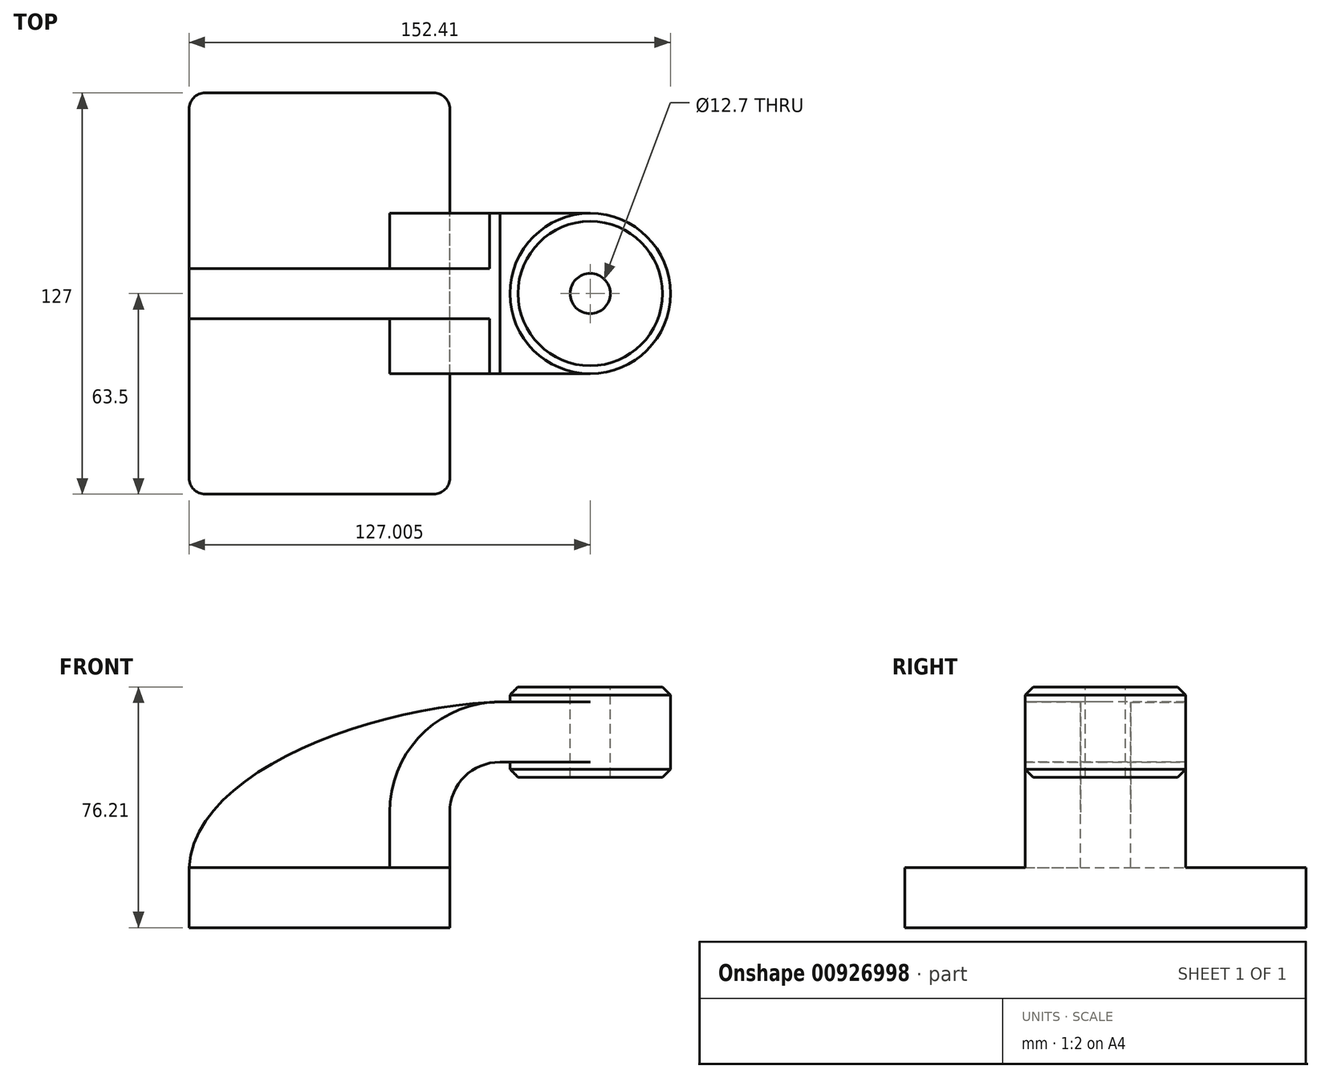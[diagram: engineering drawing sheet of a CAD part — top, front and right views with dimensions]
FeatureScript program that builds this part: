
annotation { "Feature Type Name" : "Feature", "Feature Type Description" : "" }
export const myFeature = defineFeature(function(context is Context, id is Id, definition is map)
    precondition{}
    {
        {
            var Q0;
            Q0=qCreatedBy(makeId("Front.planeOp"),FACE);
            var sketch = newSketch(context, id + "F0", { "sketchPlane" : qUnion([Q0])});
            skLineSegment(sketch, "E0.rect.bottom", {"start": v(-41.28, 9.52) * mm, "end": v(41.28, 9.52) * mm});
            skLineSegment(sketch, "E0.rect.top", {"start": v(-41.28, -9.52) * mm, "end": v(41.28, -9.52) * mm});
            skLineSegment(sketch, "E0.rect.left", {"start": v(-41.28, 9.52) * mm, "end": v(-41.28, -9.52) * mm});
            skLineSegment(sketch, "E0.rect.right", {"start": v(41.28, 9.52) * mm, "end": v(41.28, -9.52) * mm});
            skPoint(sketch, "E0.rect.middle", {"position": v(0, 0) * mm});
            skLineSegment(sketch, "E1", {"start": v(41.28, 9.52) * mm, "end": v(41.28, 27) * mm});
            skArc(sketch, "E2", {"start": v(41.28, 27) * mm, "mid": v(45.92, 38.23) * mm, "end": v(57.15, 42.88) * mm});
            skLineSegment(sketch, "E3", {"start": v(57.15, 42.88) * mm, "end": v(85.72, 42.88) * mm});
            skLineSegment(sketch, "E4.rect.bottom", {"start": v(60.32, 38.1) * mm, "end": v(111.12, 38.1) * mm});
            skLineSegment(sketch, "E4.rect.top", {"start": v(60.32, 66.68) * mm, "end": v(111.12, 66.68) * mm});
            skLineSegment(sketch, "E4.rect.left", {"start": v(60.32, 38.1) * mm, "end": v(60.32, 66.68) * mm});
            skLineSegment(sketch, "E4.rect.right", {"start": v(111.13, 38.1) * mm, "end": v(111.12, 66.68) * mm});
            skPoint(sketch, "E4.rect.middle", {"position": v(85.72, 52.39) * mm});
            skLineSegment(sketch, "E5.0", {"start": v(57.15, 61.93) * mm, "end": v(85.72, 61.93) * mm});
            skArc(sketch, "E5.1", {"start": v(22.23, 27) * mm, "mid": v(32.45, 51.7) * mm, "end": v(57.15, 61.93) * mm});
            skLineSegment(sketch, "E5.2", {"start": v(22.23, 9.52) * mm, "end": v(22.23, 27) * mm});
            skLineSegment(sketch, "E6", {"start": v(85.72, 38.1) * mm, "end": v(85.72, 66.68) * mm});
            skFitSpline(sketch, "E7", {"points": [v(-41.28, 9.53) * mm, v(57.15, 61.93) * mm], "startDerivative": vector(5.2, 92.34) * mm, "endDerivative": vector(120.92, 4.22) * mm});
            skSolve(sketch);
        }
        {
            var Q0;
            Q0=makeQuery(id+"F0.imprint","IMPRINT",FACE,{"disambiguationData":[TD([[makeQuery(id+"F0.imprint","IMPRINT",EDGE,{"derivedFrom":sQuery(id+"F0.wireOp",EDGE,"E0.rect.top")}),1.0]])]});
            extrude(context, id + "F1", {"entities" : qUnion([Q0]), "endBound" : BoundingType.SYMMETRIC, "depth" : 127 * mm});
        }
        {
            var Q0;
            {var subQ9=sQuery(id+"F0.wireOp",EDGE,"E1");Q0=makeQuery(id+"F0.imprint","IMPRINT",FACE,{"disambiguationData":[TD([[makeQuery(id+"F0.imprint","IMPRINT",EDGE,{"derivedFrom":subQ9}),1.0]])]});}
            var Q1;
            {var subQ0=sQuery(id+"F0.wireOp",EDGE,"E6");var subQ1=sQuery(id+"F0.wireOp",EDGE,"E3");var subQ2=makeQuery(id+"F0.imprint","INTERSECT",VERTEX,{"derivedFrom":[subQ1,subQ0]});Q1=makeQuery(id+"F0.imprint","IMPRINT",FACE,{"disambiguationData":[TD([[makeQuery(id+"F0.imprint","IMPRINT",EDGE,{"disambiguationData":[TD([[subQ2,1.0]])],"derivedFrom":subQ1}),1.0]])]});}
            extrude(context, id + "F2", {"entities" : qUnion([Q0, Q1]), "operationType" : NewBodyOperationType.ADD, "endBound" : BoundingType.SYMMETRIC, "depth" : 50.8 * mm});
        }
        {
            var Q0;
            {var subQ3=sQuery(id+"F0.wireOp",EDGE,"E5.2");Q0=makeQuery(id+"F0.imprint","IMPRINT",FACE,{"disambiguationData":[TD([[makeQuery(id+"F0.imprint","IMPRINT",EDGE,{"derivedFrom":subQ3}),1.0]])]});}
            extrude(context, id + "F3", {"entities" : qUnion([Q0]), "operationType" : NewBodyOperationType.ADD, "endBound" : BoundingType.SYMMETRIC, "depth" : 15.88 * mm});
        }
        {
            var Q0;
            {var subQ5=sQuery(id+"F0.wireOp",EDGE,"E4.rect.right");Q0=makeQuery(id+"F0.imprint","IMPRINT",FACE,{"disambiguationData":[TD([[makeQuery(id+"F0.imprint","IMPRINT",EDGE,{"derivedFrom":subQ5}),1.0]])]});}
            var Q1;
            Q1=sQuery(id+"F0.wireOp",EDGE,"E6");
            revolve(context, id + "F4", {"operationType" : NewBodyOperationType.ADD, "entities" : qUnion([Q0]), "axis" : qUnion([Q1]), "revolveType" : RevolveType.FULL});
        }
        {
            var Q0;
            Q0=makeQuery(id+"F1.opExtrude","CAP_EDGE",EDGE,{"disambiguationData":[OSD([sQuery(id+"F0.wireOp",EDGE,"E0.rect.right")])],"isStart":false});
            var Q1;
            Q1=makeQuery(id+"F1.opExtrude","CAP_EDGE",EDGE,{"disambiguationData":[OSD([sQuery(id+"F0.wireOp",EDGE,"E0.rect.left")])],"isStart":false});
            var Q2;
            Q2=makeQuery(id+"F1.opExtrude","CAP_EDGE",EDGE,{"disambiguationData":[OSD([sQuery(id+"F0.wireOp",EDGE,"E0.rect.right")])],"isStart":true});
            var Q3;
            Q3=makeQuery(id+"F1.opExtrude","CAP_EDGE",EDGE,{"disambiguationData":[OSD([sQuery(id+"F0.wireOp",EDGE,"E0.rect.left")])],"isStart":true});
            fillet(context, id + "F5", {"entities" : qUnion([Q0, Q1, Q2, Q3]), "radius" : 5.08 * mm, "tangentPropagation" : true, "allowEdgeOverflow" : false});
        }
        {
            var Q0;
            Q0=makeQuery(id+"F4.opRevolve","SWEPT_FACE",FACE,{"disambiguationData":[OSD([sQuery(id+"F0.wireOp",EDGE,"E4.rect.top")])]});
            var sketch = newSketch(context, id + "F6", { "sketchPlane" : qUnion([Q0])});
            skPoint(sketch, "E8", {"position": v(85.72, 0) * mm});
            skSolve(sketch);
        }
        {
            var Q0;
            Q0=sQuery(id+"F6.wireOp",VERTEX,"E8");
            var Q1;
            Q1=makeQuery(id+"F1.opExtrude","SWEPT_BODY",BODY,{"disambiguationData":[OSD([sQuery(id+"F0.wireOp",EDGE,"E0.rect.bottom"),sQuery(id+"F0.wireOp",EDGE,"E0.rect.top"),sQuery(id+"F0.wireOp",EDGE,"E0.rect.left"),sQuery(id+"F0.wireOp",EDGE,"E0.rect.right")])]});
            hole(context, id + "F7", {"style" : HoleStyle.SIMPLE, "endStyle" : HoleEndStyle.THROUGH, "holeDiameter" : 12.7 * mm, "majorDiameter" : 6.35 * mm, "isTappedThrough" : true, "tappedDepth" : 12.7 * mm, "tapClearance" : 3, "locations" : qUnion([Q0]), "scope" : qUnion([Q1])});
        }
        {
            var Q0;
            Q0=makeQuery(id+"F4.opRevolve","SWEPT_EDGE",EDGE,{"disambiguationData":[OSD([sQuery(id+"F0.wireOp",EDGE,"E4.rect.top"),sQuery(id+"F0.wireOp",EDGE,"E4.rect.right")])]});
            var Q1;
            Q1=makeQuery(id+"F4.opRevolve","SWEPT_EDGE",EDGE,{"disambiguationData":[OSD([sQuery(id+"F0.wireOp",EDGE,"E4.rect.bottom"),sQuery(id+"F0.wireOp",EDGE,"E4.rect.right")])]});
            var Q2;
            Q2=makeQuery(id+"F7.hole-0.boolean.opBoolean","COPY",EDGE,{"derivedFrom":makeQuery(id+"F7.hole-0.opRevolve","SWEPT_EDGE",EDGE,{"disambiguationData":[OSD([sQuery(id+"F7.hole-0.sketch.wireOp",EDGE,"core_line_2"),sQuery(id+"F7.hole-0.sketch.wireOp",EDGE,"core_line_3")])]})});
            var Q3;
            Q3=makeQuery(id+"F7.hole-0.boolean.opBoolean","INTERSECT",EDGE,{"derivedFrom":[makeQuery(id+"F4.opRevolve","SWEPT_FACE",FACE,{"disambiguationData":[OSD([sQuery(id+"F0.wireOp",EDGE,"E4.rect.bottom")])]}),makeQuery(id+"F7.hole-0.opRevolve","SWEPT_FACE",FACE,{"disambiguationData":[OSD([sQuery(id+"F7.hole-0.sketch.wireOp",EDGE,"core_line_2")])]})]});
            chamfer(context, id + "F8", {"entities" : qUnion([Q0, Q1, Q2, Q3]), "width" : 2.54 * mm, "tangentPropagation" : true});
        }
    });
